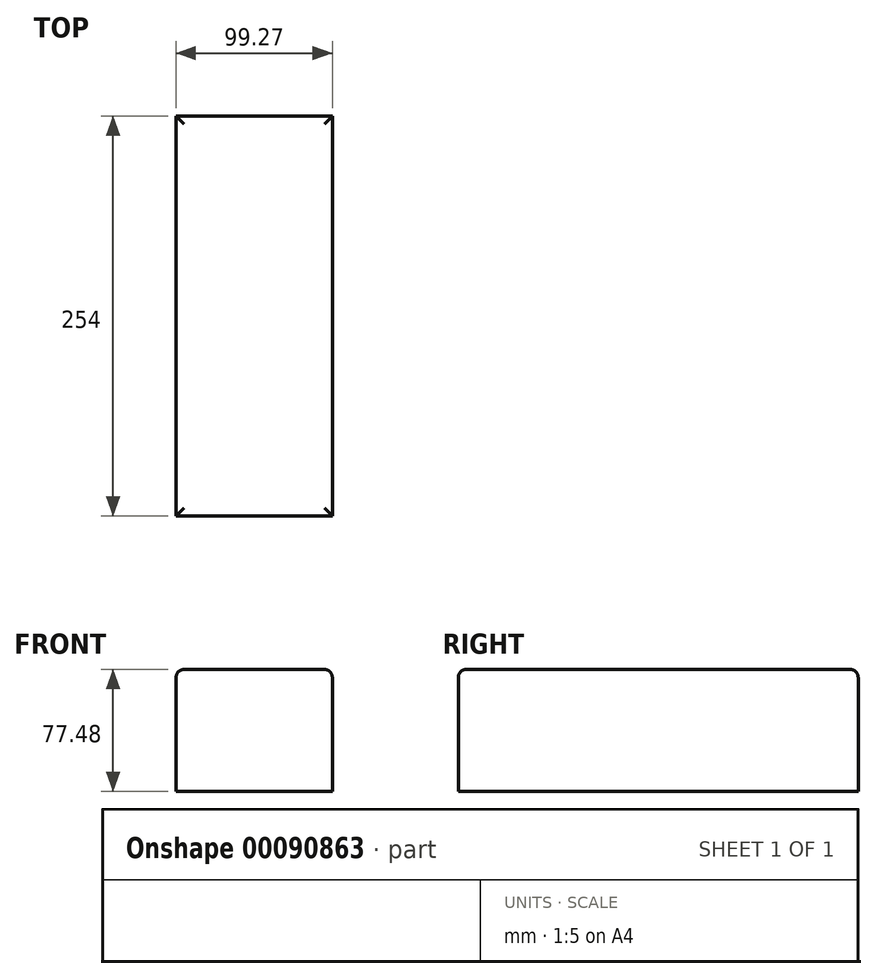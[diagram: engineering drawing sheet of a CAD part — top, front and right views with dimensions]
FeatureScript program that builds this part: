
annotation { "Feature Type Name" : "Feature", "Feature Type Description" : "" }
export const myFeature = defineFeature(function(context is Context, id is Id, definition is map)
    precondition{}
    {
        {
            var Q0;
            Q0=qCreatedBy(makeId("Front.planeOp"),FACE);
            var sketch = newSketch(context, id + "F0", { "sketchPlane" : qUnion([Q0])});
            skLineSegment(sketch, "E0.bottom", {"start": v(-45.7, 26.48) * mm, "end": v(53.57, 26.48) * mm});
            skLineSegment(sketch, "E0.top", {"start": v(-45.7, -51) * mm, "end": v(53.57, -51) * mm});
            skLineSegment(sketch, "E0.left", {"start": v(-45.7, 26.48) * mm, "end": v(-45.7, -51) * mm});
            skLineSegment(sketch, "E0.right", {"start": v(53.57, 26.48) * mm, "end": v(53.57, -51) * mm});
            skSolve(sketch);
        }
        {
            var Q0;
            Q0 = qSketchRegion(id + "F0", true);
            extrude(context, id + "F1", {"entities" : qUnion([Q0]), "endBound" : BoundingType.SYMMETRIC, "depth" : 254 * mm});
        }
        {
            var Q0;
            Q0=makeQuery(id+"F1.opExtrude","SWEPT_EDGE",EDGE,{"disambiguationData":[OSD([sQuery(id+"F0.wireOp",EDGE,"E0.bottom"),sQuery(id+"F0.wireOp",EDGE,"E0.right")])]});
            var Q1;
            Q1=makeQuery(id+"F1.opExtrude","CAP_EDGE",EDGE,{"disambiguationData":[OSD([sQuery(id+"F0.wireOp",EDGE,"E0.bottom")])],"isStart":false});
            var Q2;
            Q2=makeQuery(id+"F1.opExtrude","SWEPT_EDGE",EDGE,{"disambiguationData":[OSD([sQuery(id+"F0.wireOp",EDGE,"E0.bottom"),sQuery(id+"F0.wireOp",EDGE,"E0.left")])]});
            var Q3;
            Q3=makeQuery(id+"F1.opExtrude","CAP_EDGE",EDGE,{"disambiguationData":[OSD([sQuery(id+"F0.wireOp",EDGE,"E0.bottom")])],"isStart":true});
            fillet(context, id + "F2", {"entities" : qUnion([Q0, Q1, Q2, Q3]), "radius" : 5.08 * mm, "tangentPropagation" : true, "allowEdgeOverflow" : false});
        }
    });
